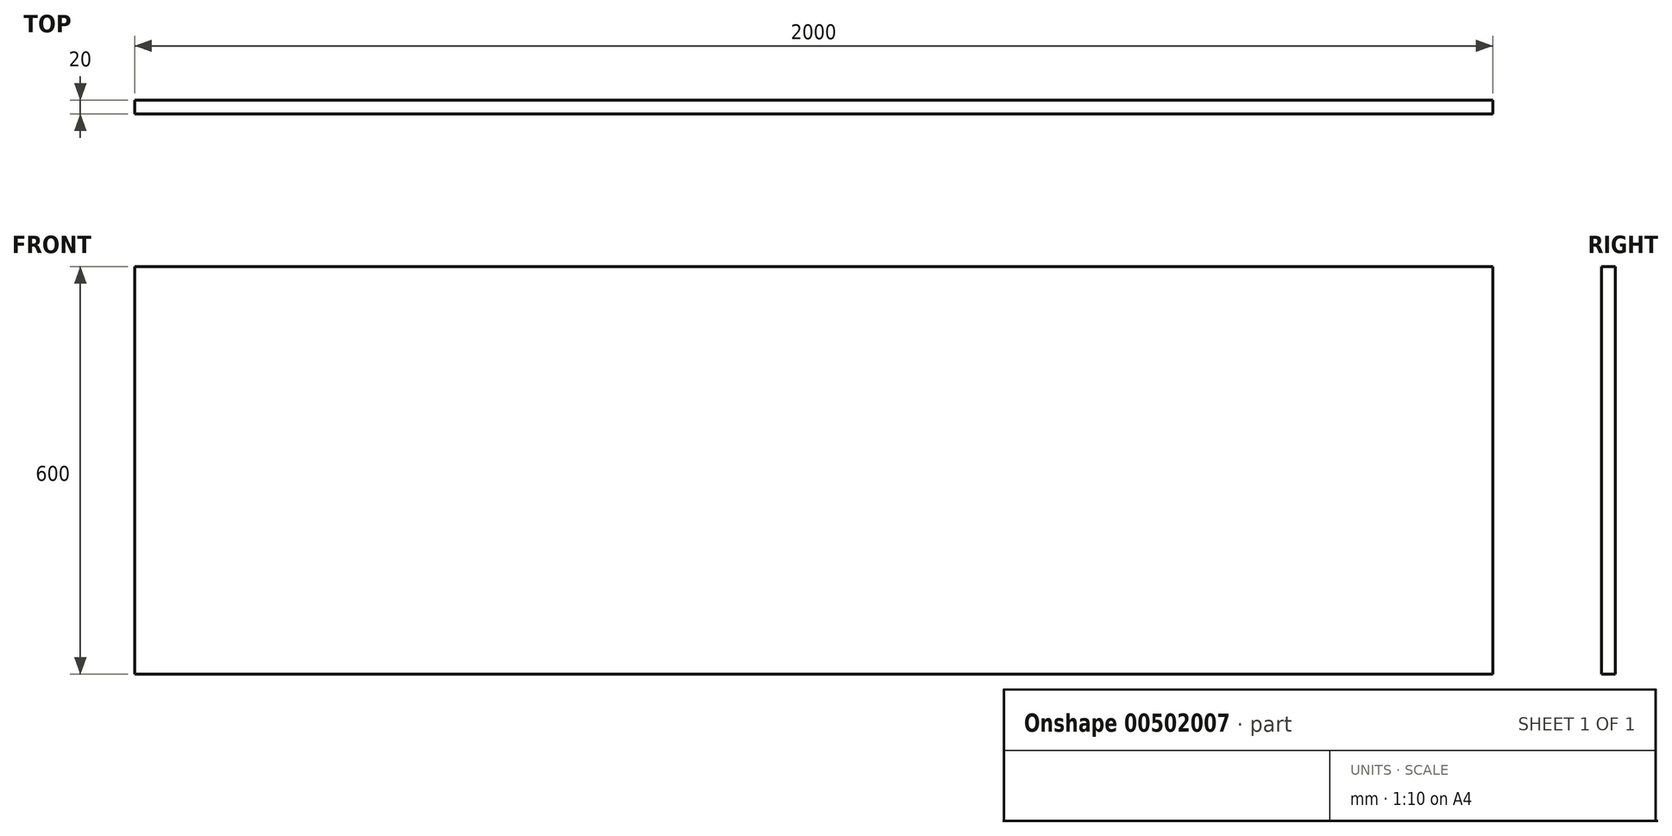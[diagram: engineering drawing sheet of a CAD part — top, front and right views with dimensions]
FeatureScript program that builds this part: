
annotation { "Feature Type Name" : "Feature", "Feature Type Description" : "" }
export const myFeature = defineFeature(function(context is Context, id is Id, definition is map)
    precondition{}
    {
        {
            var Q0;
            Q0=qCreatedBy(makeId("Front.planeOp"),FACE);
            var sketch = newSketch(context, id + "F0", { "sketchPlane" : qUnion([Q0])});
            skLineSegment(sketch, "E0.bottom", {"start": v(0, 0) * mm, "end": v(2000, 0) * mm});
            skLineSegment(sketch, "E0.top", {"start": v(0, 600) * mm, "end": v(2000, 600) * mm});
            skLineSegment(sketch, "E0.left", {"start": v(0, 0) * mm, "end": v(0, 600) * mm});
            skLineSegment(sketch, "E0.right", {"start": v(2000, 0) * mm, "end": v(2000, 600) * mm});
            skSolve(sketch);
        }
        {
            var Q0;
            Q0 = qSketchRegion(id + "F0", true);
            extrude(context, id + "F1", {"entities" : qUnion([Q0]), "depth" : 20 * mm});
        }
    });
